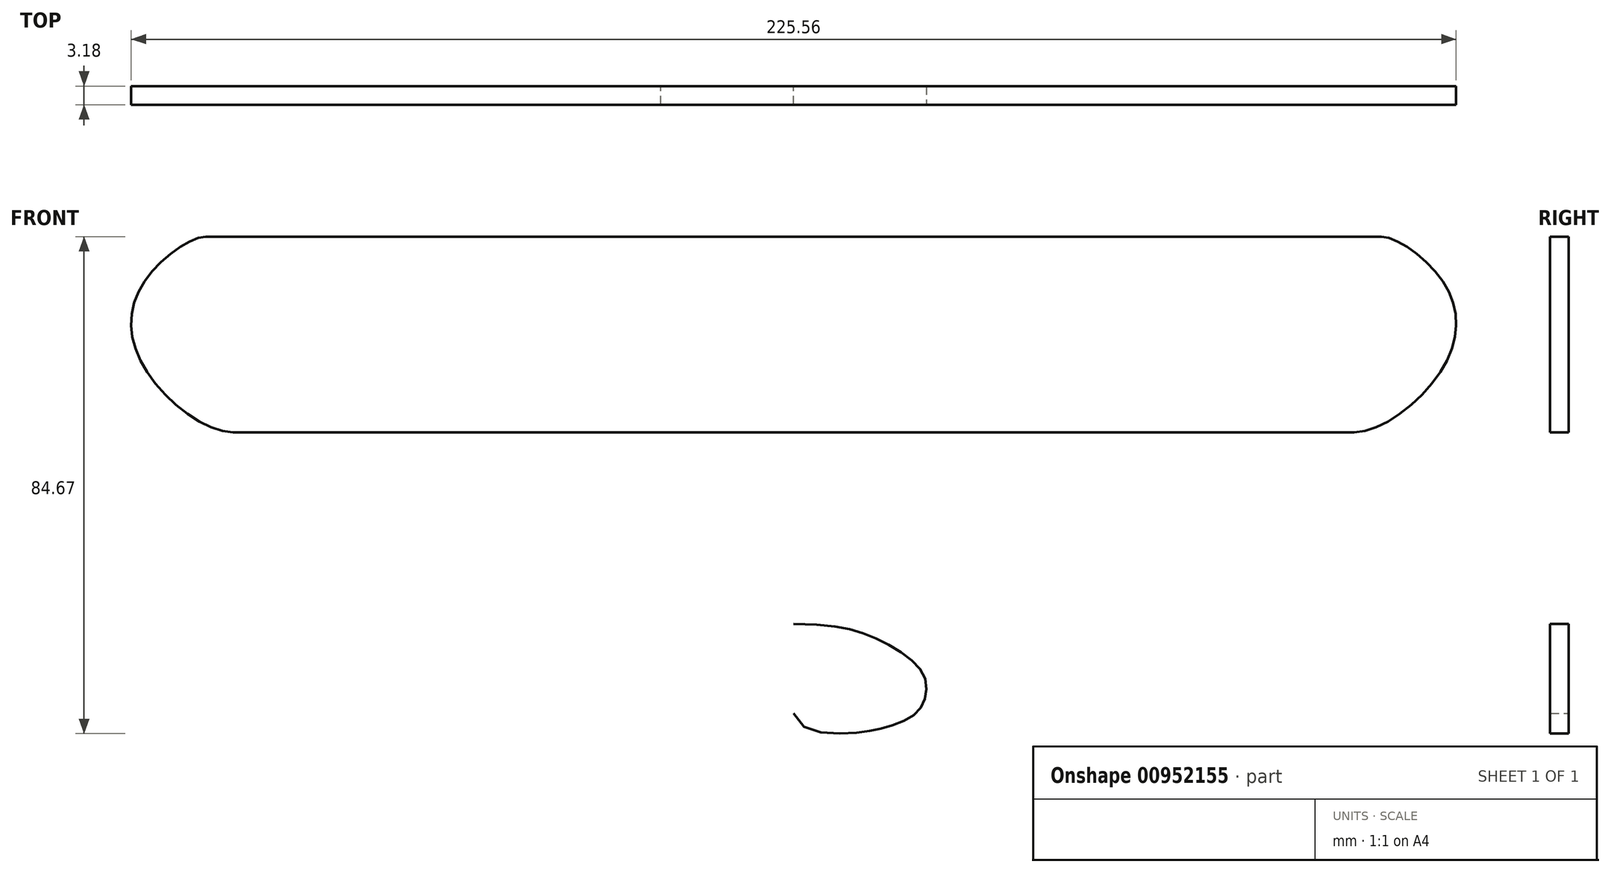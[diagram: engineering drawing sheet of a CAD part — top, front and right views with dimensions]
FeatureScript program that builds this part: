
annotation { "Feature Type Name" : "Feature", "Feature Type Description" : "" }
export const myFeature = defineFeature(function(context is Context, id is Id, definition is map)
    precondition{}
    {
        {
            var Q0;
            Q0=qCreatedBy(makeId("Front.planeOp"),FACE);
            var sketch = newSketch(context, id + "F0", { "sketchPlane" : qUnion([Q0])});
            skLineSegment(sketch, "E0.bottom", {"start": v(114.3, 50.8) * mm, "end": v(-114.3, 50.8) * mm, "construction": true});
            skLineSegment(sketch, "E0.top", {"start": v(114.3, -50.8) * mm, "end": v(-114.3, -50.8) * mm, "construction": true});
            skLineSegment(sketch, "E0.left", {"start": v(114.3, 50.8) * mm, "end": v(114.3, -50.8) * mm, "construction": true});
            skLineSegment(sketch, "E0.right", {"start": v(-114.3, 50.8) * mm, "end": v(-114.3, -50.8) * mm, "construction": true});
            skPoint(sketch, "E0.middle", {"position": v(0, 0) * mm});
            skLineSegment(sketch, "E1", {"start": v(0, 15.55) * mm, "end": v(95.45, 15.55) * mm});
            skLineSegment(sketch, "E2", {"start": v(0, 48.86) * mm, "end": v(100.08, 48.86) * mm});
            skFitSpline(sketch, "E3", {"points": [v(100.08, 48.86) * mm, v(110.61, 41.1) * mm, v(110.73, 26.87) * mm, v(95.45, 15.55) * mm], "startDerivative": vector(25.66, 0) * mm, "endDerivative": vector(-39.76, 0) * mm});
            skLineSegment(sketch, "E4", {"start": v(0, -17.09) * mm, "end": v(0, -32.33) * mm, "construction": true});
            skFitSpline(sketch, "E5.MirrorCS", {"points": [v(-100.08, 48.86) * mm, v(-110.61, 41.1) * mm, v(-110.73, 26.87) * mm, v(-95.45, 15.55) * mm], "startDerivative": vector(-25.66, 0) * mm, "endDerivative": vector(39.76, 0) * mm});
            skLineSegment(sketch, "E6.MirrorCS", {"start": v(0, 48.86) * mm, "end": v(-100.08, 48.86) * mm});
            skLineSegment(sketch, "E7.MirrorCS", {"start": v(0, 15.55) * mm, "end": v(-95.45, 15.55) * mm});
            skFitSpline(sketch, "E8", {"points": [v(0, -17.09) * mm, v(11.48, -18.58) * mm, v(18.15, -21.86) * mm, v(22.16, -25.88) * mm, v(22.38, -29.68) * mm, v(20.47, -32.65) * mm, v(15.6, -34.76) * mm, v(9.79, -35.7) * mm, v(0, -32.33) * mm], "startDerivative": vector(103.39, -2) * mm, "endDerivative": vector(-23.02, 70.9) * mm});
            skFitSpline(sketch, "E9.MirrorCS", {"points": [v(0, -17.09) * mm, v(-11.48, -18.58) * mm, v(-18.15, -21.86) * mm, v(-22.16, -25.88) * mm, v(-22.38, -29.68) * mm, v(-20.47, -32.65) * mm, v(-15.6, -34.76) * mm, v(-9.79, -35.7) * mm, v(0, -32.33) * mm], "startDerivative": vector(-103.39, -2) * mm, "endDerivative": vector(23.02, 70.9) * mm});
            skSolve(sketch);
        }
        {
            var Q0;
            Q0=makeQuery(id+"F0.imprint","IMPRINT",FACE,{"disambiguationData":[TD([[makeQuery(id+"F0.imprint","IMPRINT",EDGE,{"derivedFrom":sQuery(id+"F0.wireOp",EDGE,"E1")}),1.0]])]});
            var Q1;
            Q1=makeQuery(id+"F0.imprint","IMPRINT",FACE,{"disambiguationData":[TD([[makeQuery(id+"F0.imprint","IMPRINT",EDGE,{"derivedFrom":sQuery(id+"F0.wireOp",EDGE,"E8")}),-1.0]])]});
            extrude(context, id + "F1", {"entities" : qUnion([Q0, Q1]), "endBound" : BoundingType.SYMMETRIC, "depth" : 3.17 * mm, "offsetDistance" : 25.4 * mm});
        }
    });
